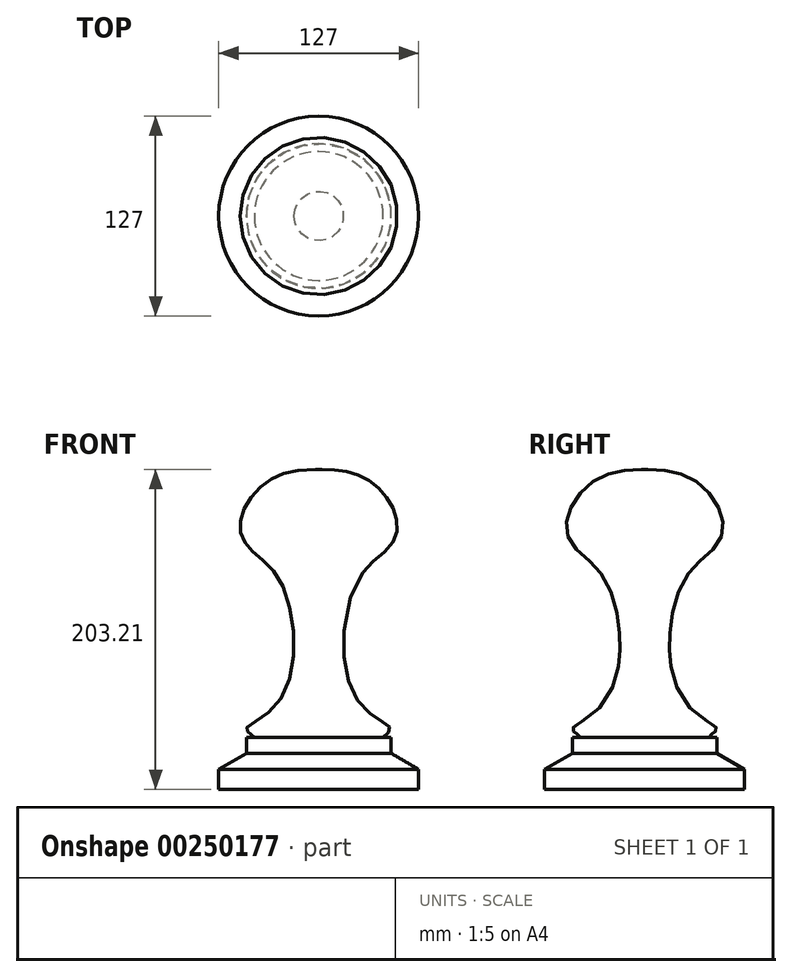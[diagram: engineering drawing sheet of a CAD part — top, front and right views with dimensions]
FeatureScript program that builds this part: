
annotation { "Feature Type Name" : "Feature", "Feature Type Description" : "" }
export const myFeature = defineFeature(function(context is Context, id is Id, definition is map)
    precondition{}
    {
        {
            var Q0;
            Q0=qCreatedBy(makeId("Front.planeOp"),FACE);
            var sketch = newSketch(context, id + "F0", { "sketchPlane" : qUnion([Q0])});
            skLineSegment(sketch, "E0", {"start": v(-56.46, -57.93) * mm, "end": v(7.04, -57.93) * mm});
            skLineSegment(sketch, "E1", {"start": v(7.04, -57.93) * mm, "end": v(7.04, 145.27) * mm});
            skLineSegment(sketch, "E2", {"start": v(-56.46, -57.93) * mm, "end": v(-56.46, -45.23) * mm});
            skLineSegment(sketch, "E3", {"start": v(-56.46, -45.23) * mm, "end": v(-38.94, -34.95) * mm});
            skLineSegment(sketch, "E4", {"start": v(-38.94, -34.95) * mm, "end": v(-38.94, -24.79) * mm});
            skLineSegment(sketch, "E5", {"start": v(-38.94, -24.79) * mm, "end": v(-33.86, -24.79) * mm});
            skFitSpline(sketch, "E6", {"points": [v(-33.86, -24.79) * mm, v(-38.94, -19.37) * mm, v(-16.81, 0) * mm, v(-17.47, 74.34) * mm, v(-38.94, 97.48) * mm, v(-42.05, 115.5) * mm, v(-26.04, 137.5) * mm, v(7.04, 145.27) * mm], "startDerivative": vector(-106.87, 132.83) * mm, "endDerivative": vector(290.21, -4.29) * mm});
            skLineSegment(sketch, "E7", {"start": v(7.04, 179.07) * mm, "end": v(7.04, -109.98) * mm, "construction": true});
            skSolve(sketch);
        }
        {
            var Q0;
            Q0=makeQuery(id+"F0.imprint","IMPRINT",FACE,{"disambiguationData":[TD([[makeQuery(id+"F0.imprint","IMPRINT",EDGE,{"derivedFrom":sQuery(id+"F0.wireOp",EDGE,"E0")}),1.0]])]});
            var Q1;
            Q1=sQuery(id+"F0.wireOp",EDGE,"E7");
            revolve(context, id + "F1", {"entities" : qUnion([Q0]), "axis" : qUnion([Q1]), "revolveType" : RevolveType.FULL});
        }
    });
